# Revit family: Shower_Head-Grohe-Rainshower_F_Series-27468000
name_source: partatom
category: Plumbing Fixtures
revit_build: Autodesk Revit 2018 (Build: 20170223_1515(x64)
units: mm (PartAtom-declared; Revit-internal decimal feet)

## family parameters
Always vertical = No
Cut with Voids When Loaded = No
OmniClass Number = 23.45.05.14.17
OmniClass Title = Showers
Part Type = Normal
Room Calculation Point = No
Round Connector Dimension = Use Diameter
Shared = Yes
Work Plane-Based = Yes

## types (1)
- 27468000
    Assembly Code = D2010710
    CW Connection = No
    CWFU = 3
    Default Elevation = 74"
    Depth = 2 5/16"
    Depth Input = 0"
    Description = Rainshower® F-Series 10inch Ceiling Shower Head, GROHE StarLight chrome finish, GROHE DreamSpray perfect 1-rain spray pattern with 120 spray nozzles, SpeedClean anti-lime system and Suitable for instantaneous heater.
    Finish = Metal-Grohe-000-StarLight Chrome
    Flow Rate = 2.5 gpm (9.5 l/min) Flow Limiter
    HW Connection = No
    HWFU = 3
    Height = 1/2"
    IAPMO Compliance = Energy Policy Act of 1992, ASME A112.18.1/CSA B125.1
    Installation Type = Flush Mount
    Manufacturer = Grohe
    Material = Metal-Grohe-000-StarLight Chrome
    Model = 27468000
    Price = Prices may vary. Please consult Manufacturer Representative for most up-to-date price list.
    Product Documentation Link = https://americanstandard.box.com
    Product Page URL = https://www.grohe.us
    Revised Date = 07/17/2021
    Tempered Water Connection = Yes
    Tempered Water Connection Diameter = 1/2"
    URL = https://www.grohe.us
    Vent Connection = No
    WFU = 4
    Waste Connection = No
    Width = 10"

## geometry (parser evidence)
native form markers: Sweep x2
no freeform markers — native parametric forms only
